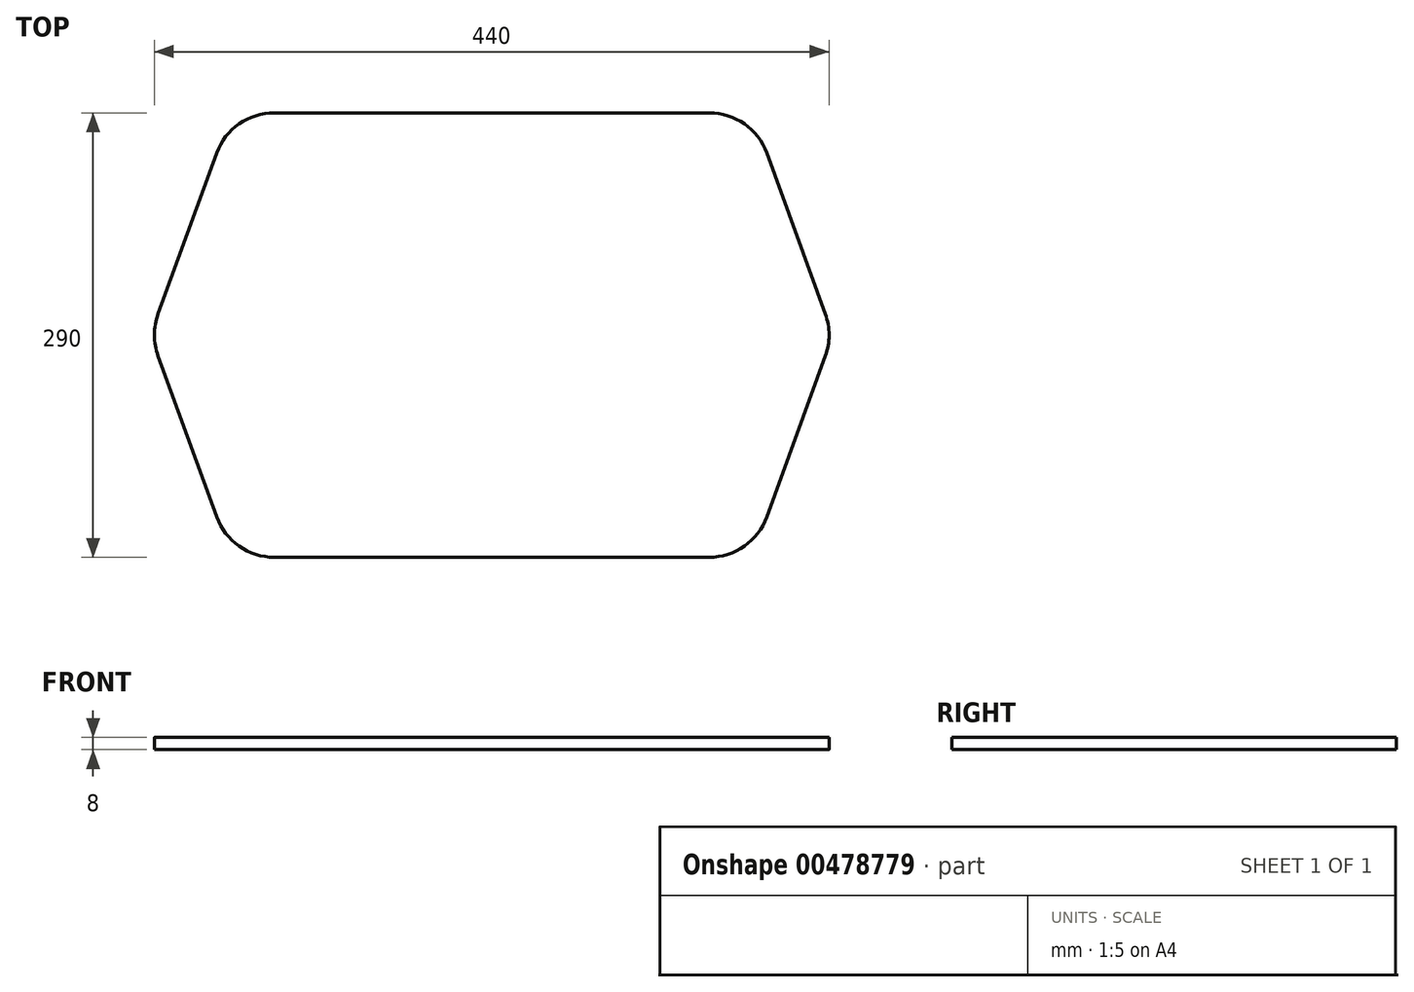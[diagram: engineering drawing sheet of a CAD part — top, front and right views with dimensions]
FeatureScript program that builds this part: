
annotation { "Feature Type Name" : "Feature", "Feature Type Description" : "" }
export const myFeature = defineFeature(function(context is Context, id is Id, definition is map)
    precondition{}
    {
        {
            var Q0;
            Q0=qCreatedBy(makeId("Top.planeOp"),FACE);
            var sketch = newSketch(context, id + "F0", { "sketchPlane" : qUnion([Q0])});
            skArc(sketch, "E0", {"start": v(-217.59, 13.68) * mm, "mid": v(-219.4, 6.95) * mm, "end": v(-220, 0) * mm});
            skArc(sketch, "E1", {"start": v(-141.78, 145) * mm, "mid": v(-164.73, 137.77) * mm, "end": v(-179.37, 118.68) * mm});
            skLineSegment(sketch, "E2", {"start": v(0, 145) * mm, "end": v(-141.78, 145) * mm});
            skLineSegment(sketch, "E3", {"start": v(-179.37, 118.68) * mm, "end": v(-217.59, 13.68) * mm});
            skLineSegment(sketch, "E4", {"start": v(0, 0) * mm, "end": v(-220, 0) * mm, "construction": true});
            skLineSegment(sketch, "E5", {"start": v(0, 0) * mm, "end": v(0, 145) * mm, "construction": true});
            skArc(sketch, "E6.MirrorCS", {"start": v(-217.59, -13.68) * mm, "mid": v(-219.4, -6.95) * mm, "end": v(-220, 0) * mm});
            skLineSegment(sketch, "E7.MirrorCS", {"start": v(-179.37, -118.68) * mm, "end": v(-217.59, -13.68) * mm});
            skArc(sketch, "E8.MirrorCS", {"start": v(-141.78, -145) * mm, "mid": v(-164.73, -137.77) * mm, "end": v(-179.37, -118.68) * mm});
            skLineSegment(sketch, "E9.MirrorCS", {"start": v(0, -145) * mm, "end": v(-141.78, -145) * mm});
            skArc(sketch, "E10.MirrorCS", {"start": v(217.59, 13.68) * mm, "mid": v(219.4, 6.95) * mm, "end": v(220, 0) * mm});
            skArc(sketch, "E11.MirrorCS", {"start": v(141.78, 145) * mm, "mid": v(164.73, 137.77) * mm, "end": v(179.37, 118.68) * mm});
            skLineSegment(sketch, "E12.MirrorCS", {"start": v(0, 145) * mm, "end": v(141.78, 145) * mm});
            skLineSegment(sketch, "E13.MirrorCS", {"start": v(0, -145) * mm, "end": v(141.78, -145) * mm});
            skArc(sketch, "E14.MirrorCS", {"start": v(141.78, -145) * mm, "mid": v(164.73, -137.77) * mm, "end": v(179.37, -118.68) * mm});
            skLineSegment(sketch, "E15.MirrorCS", {"start": v(179.37, 118.68) * mm, "end": v(217.59, 13.68) * mm});
            skLineSegment(sketch, "E16.MirrorCS", {"start": v(179.37, -118.68) * mm, "end": v(217.59, -13.68) * mm});
            skArc(sketch, "E17.MirrorCS", {"start": v(217.59, -13.68) * mm, "mid": v(219.4, -6.95) * mm, "end": v(220, 0) * mm});
            skSolve(sketch);
        }
        {
            var Q0;
            Q0=makeQuery(id+"F0.imprint","IMPRINT",FACE,{"disambiguationData":[TD([[makeQuery(id+"F0.imprint","IMPRINT",EDGE,{"derivedFrom":sQuery(id+"F0.wireOp",EDGE,"E0")}),1.0]])]});
            extrude(context, id + "F1", {"entities" : qUnion([Q0]), "depth" : 8 * mm});
        }
    });
